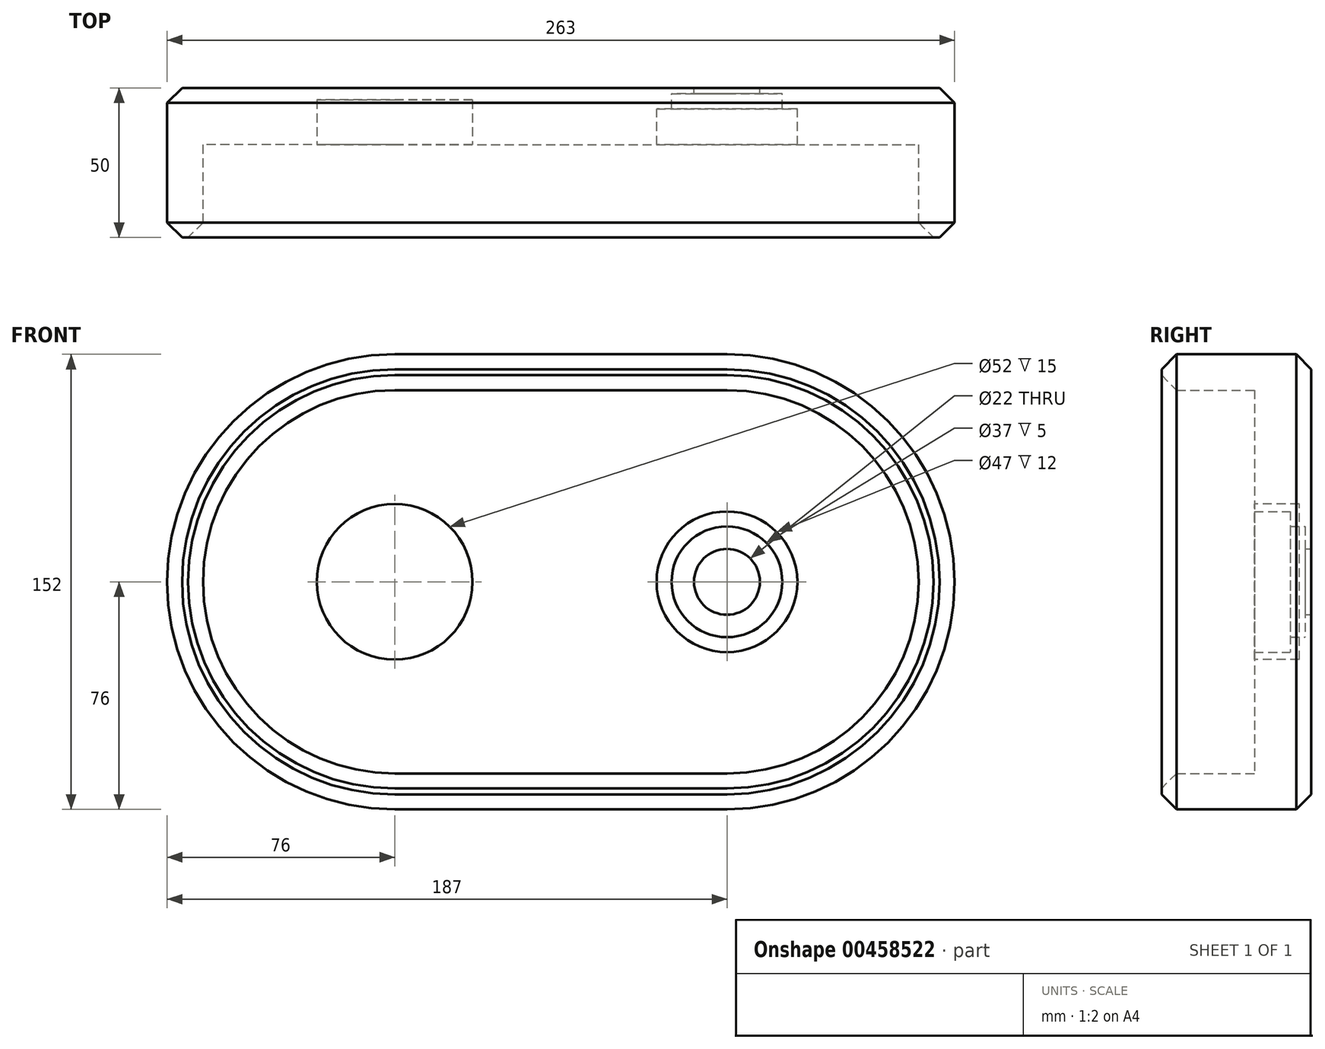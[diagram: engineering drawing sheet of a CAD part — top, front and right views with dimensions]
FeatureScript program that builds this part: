
annotation { "Feature Type Name" : "Feature", "Feature Type Description" : "" }
export const myFeature = defineFeature(function(context is Context, id is Id, definition is map)
    precondition{}
    {
        {
            var Q0;
            Q0=qCreatedBy(makeId("Front.planeOp"),FACE);
            var sketch = newSketch(context, id + "F0", { "sketchPlane" : qUnion([Q0])});
            skArc(sketch, "E0", {"start": v(0, 76) * mm, "mid": v(-76, 0) * mm, "end": v(0, -76) * mm});
            skLineSegment(sketch, "E1", {"start": v(0, 0) * mm, "end": v(204.87, 0) * mm, "construction": true});
            skArc(sketch, "E2", {"start": v(111, -76) * mm, "mid": v(187, 0) * mm, "end": v(111, 76) * mm});
            skLineSegment(sketch, "E3", {"start": v(0, 76) * mm, "end": v(111, 76) * mm});
            skLineSegment(sketch, "E4", {"start": v(0, -76) * mm, "end": v(111, -76) * mm});
            skSolve(sketch);
        }
        {
            var Q0;
            Q0=makeQuery(id+"F0.imprint","IMPRINT",FACE,{"disambiguationData":[TD([[makeQuery(id+"F0.imprint","IMPRINT",EDGE,{"derivedFrom":sQuery(id+"F0.wireOp",EDGE,"E0")}),1.0]])]});
            extrude(context, id + "F1", {"entities" : qUnion([Q0]), "depth" : 50 * mm, "offsetDistance" : 25 * mm});
        }
        {
            var Q0;
            Q0=qCreatedBy(makeId("Front.planeOp"),FACE);
            cPlane(context, id + "F2", {"entities" : qUnion([Q0]), "cplaneType" : CPlaneType.OFFSET, "offset" : 19 * mm, "width" : 150 * mm, "height" : 150 * mm});
        }
        {
            var Q0;
            Q0=qCreatedBy(id+"F2.planeOp",FACE);
            var sketch = newSketch(context, id + "F3", { "sketchPlane" : qUnion([Q0])});
            skArc(sketch, "E5", {"start": v(0, 64) * mm, "mid": v(-64, 0) * mm, "end": v(0, -64) * mm});
            skLineSegment(sketch, "E6", {"start": v(0, 0) * mm, "end": v(196.84, 0) * mm, "construction": true});
            skArc(sketch, "E7", {"start": v(111, -64) * mm, "mid": v(175, 0) * mm, "end": v(111, 64) * mm});
            skLineSegment(sketch, "E8", {"start": v(0, 64) * mm, "end": v(111, 64) * mm});
            skLineSegment(sketch, "E9", {"start": v(0, -64) * mm, "end": v(111, -64) * mm});
            skSolve(sketch);
        }
        {
            var Q0;
            Q0 = qSketchRegion(id + "F3", true);
            var Q1;
            Q1=makeQuery(id+"F1.opExtrude","CAP_FACE",FACE,{"disambiguationData":[OSD([sQuery(id+"F0.wireOp",EDGE,"E0"),sQuery(id+"F0.wireOp",EDGE,"E2"),sQuery(id+"F0.wireOp",EDGE,"E3"),sQuery(id+"F0.wireOp",EDGE,"E4")])],"isStart":false});
            extrude(context, id + "F4", {"entities" : qUnion([Q0, Q1]), "operationType" : NewBodyOperationType.REMOVE, "depth" : 60 * mm, "offsetDistance" : 25 * mm});
        }
        {
            var Q0;
            Q0=qCreatedBy(id+"F2.planeOp",FACE);
            var sketch = newSketch(context, id + "F5", { "sketchPlane" : qUnion([Q0])});
            skCircle(sketch, "E10", {"center": v(0, 0) * mm, "radius": 26 * mm});
            skSolve(sketch);
        }
        {
            var Q0;
            Q0 = qSketchRegion(id + "F5", true);
            var Q1;
            Q1=makeQuery(id+"F5.imprint","IMPRINT",FACE,{"disambiguationData":[TD([[makeQuery(id+"F5.imprint","IMPRINT",EDGE,{"derivedFrom":sQuery(id+"F5.wireOp",EDGE,"E10")}),1.0]])]});
            extrude(context, id + "F6", {"entities" : qUnion([Q0, Q1]), "operationType" : NewBodyOperationType.REMOVE, "oppositeDirection" : true, "depth" : 15 * mm, "offsetDistance" : 25 * mm});
        }
        {
            var Q0;
            Q0=qCreatedBy(makeId("Right.planeOp"),FACE);
            cPlane(context, id + "F7", {"entities" : qUnion([Q0]), "cplaneType" : CPlaneType.OFFSET, "offset" : 111 * mm, "width" : 150 * mm, "height" : 150 * mm});
        }
        {
            var Q0;
            Q0=qCreatedBy(id+"F7.planeOp",FACE);
            var sketch = newSketch(context, id + "F8", { "sketchPlane" : qUnion([Q0])});
            skLineSegment(sketch, "E11", {"start": v(0, 11) * mm, "end": v(-2, 11) * mm});
            skLineSegment(sketch, "E12", {"start": v(-2, 11) * mm, "end": v(-2, 18.5) * mm});
            skLineSegment(sketch, "E13", {"start": v(-2, 18.5) * mm, "end": v(-7, 18.5) * mm});
            skLineSegment(sketch, "E14", {"start": v(-7, 18.5) * mm, "end": v(-7, 23.5) * mm});
            skLineSegment(sketch, "E15", {"start": v(-7, 23.5) * mm, "end": v(-19, 23.5) * mm});
            skLineSegment(sketch, "E16", {"start": v(-19, 23.5) * mm, "end": v(-19, 0) * mm});
            skLineSegment(sketch, "E17", {"start": v(-19, 0) * mm, "end": v(0, 0) * mm, "construction": true});
            skLineSegment(sketch, "E18", {"start": v(0, 0) * mm, "end": v(0, 11) * mm});
            skLineSegment(sketch, "E19", {"start": v(-19, 0) * mm, "end": v(0, 0) * mm});
            skSolve(sketch);
        }
        {
            var Q0;
            Q0 = qSketchRegion(id + "F8", true);
            var Q1;
            Q1=sQuery(id+"F8.wireOp",EDGE,"E17");
            revolve(context, id + "F9", {"operationType" : NewBodyOperationType.REMOVE, "entities" : qUnion([Q0]), "axis" : qUnion([Q1]), "revolveType" : RevolveType.FULL, "oppositeDirection" : true});
        }
        {
            var Q0;
            Q0=makeQuery(id+"F1.opExtrude","CAP_EDGE",EDGE,{"disambiguationData":[OSD([sQuery(id+"F0.wireOp",EDGE,"E3")])],"isStart":true});
            var Q1;
            Q1=makeQuery(id+"F1.opExtrude","CAP_EDGE",EDGE,{"disambiguationData":[OSD([sQuery(id+"F0.wireOp",EDGE,"E2")])],"isStart":true});
            var Q2;
            Q2=makeQuery(id+"F1.opExtrude","CAP_EDGE",EDGE,{"disambiguationData":[OSD([sQuery(id+"F0.wireOp",EDGE,"E0")])],"isStart":true});
            var Q3;
            Q3=makeQuery(id+"F1.opExtrude","CAP_EDGE",EDGE,{"disambiguationData":[OSD([sQuery(id+"F0.wireOp",EDGE,"E4")])],"isStart":true});
            chamfer(context, id + "F10", {"entities" : qUnion([Q0, Q1, Q2, Q3]), "width" : 5 * mm, "tangentPropagation" : true});
        }
        {
            var Q0;
            Q0=makeQuery(id+"F1.opExtrude","CAP_EDGE",EDGE,{"disambiguationData":[OSD([sQuery(id+"F0.wireOp",EDGE,"E3")])],"isStart":false});
            var Q1;
            Q1=makeQuery(id+"F1.opExtrude","CAP_EDGE",EDGE,{"disambiguationData":[OSD([sQuery(id+"F0.wireOp",EDGE,"E0")])],"isStart":false});
            var Q2;
            Q2=makeQuery(id+"F1.opExtrude","CAP_EDGE",EDGE,{"disambiguationData":[OSD([sQuery(id+"F0.wireOp",EDGE,"E2")])],"isStart":false});
            var Q3;
            Q3=makeQuery(id+"F1.opExtrude","CAP_EDGE",EDGE,{"disambiguationData":[OSD([sQuery(id+"F0.wireOp",EDGE,"E4")])],"isStart":false});
            chamfer(context, id + "F11", {"entities" : qUnion([Q0, Q1, Q2, Q3]), "width" : 5 * mm, "tangentPropagation" : true});
        }
        {
            var Q0;
            {var subQ0=sQuery(id+"F0.wireOp",EDGE,"E4");var subQ1=sQuery(id+"F0.wireOp",EDGE,"E3");var subQ2=sQuery(id+"F0.wireOp",EDGE,"E2");var subQ3=sQuery(id+"F0.wireOp",EDGE,"E0");Q0=makeQuery(id+"F4.boolean.opBoolean","INTERSECT",EDGE,{"derivedFrom":[makeQuery(id+"F1.opExtrude","CAP_FACE",FACE,{"disambiguationData":[OSD([subQ3,subQ2,subQ1,subQ0])],"isStart":false}),makeQuery(id+"F4.opExtrude","CAP_FACE",FACE,{"disambiguationData":[OSD([subQ3,subQ2,subQ1,subQ0])],"isStart":true}),makeQuery(id+"F4.opExtrude","SWEPT_FACE",FACE,{"disambiguationData":[OSD([sQuery(id+"F3.wireOp",EDGE,"E8")])]})]});}
            var Q1;
            {var subQ0=sQuery(id+"F0.wireOp",EDGE,"E4");var subQ1=sQuery(id+"F0.wireOp",EDGE,"E3");var subQ2=sQuery(id+"F0.wireOp",EDGE,"E2");var subQ3=sQuery(id+"F0.wireOp",EDGE,"E0");Q1=makeQuery(id+"F4.boolean.opBoolean","INTERSECT",EDGE,{"derivedFrom":[makeQuery(id+"F1.opExtrude","CAP_FACE",FACE,{"disambiguationData":[OSD([subQ3,subQ2,subQ1,subQ0])],"isStart":false}),makeQuery(id+"F4.opExtrude","CAP_FACE",FACE,{"disambiguationData":[OSD([subQ3,subQ2,subQ1,subQ0])],"isStart":true}),makeQuery(id+"F4.opExtrude","SWEPT_FACE",FACE,{"disambiguationData":[OSD([sQuery(id+"F3.wireOp",EDGE,"E5")])]})]});}
            var Q2;
            {var subQ0=sQuery(id+"F0.wireOp",EDGE,"E4");var subQ1=sQuery(id+"F0.wireOp",EDGE,"E3");var subQ2=sQuery(id+"F0.wireOp",EDGE,"E2");var subQ3=sQuery(id+"F0.wireOp",EDGE,"E0");Q2=makeQuery(id+"F4.boolean.opBoolean","INTERSECT",EDGE,{"derivedFrom":[makeQuery(id+"F1.opExtrude","CAP_FACE",FACE,{"disambiguationData":[OSD([subQ3,subQ2,subQ1,subQ0])],"isStart":false}),makeQuery(id+"F4.opExtrude","CAP_FACE",FACE,{"disambiguationData":[OSD([subQ3,subQ2,subQ1,subQ0])],"isStart":true}),makeQuery(id+"F4.opExtrude","SWEPT_FACE",FACE,{"disambiguationData":[OSD([sQuery(id+"F3.wireOp",EDGE,"E7")])]})]});}
            var Q3;
            {var subQ0=sQuery(id+"F0.wireOp",EDGE,"E4");var subQ1=sQuery(id+"F0.wireOp",EDGE,"E3");var subQ2=sQuery(id+"F0.wireOp",EDGE,"E2");var subQ3=sQuery(id+"F0.wireOp",EDGE,"E0");Q3=makeQuery(id+"F4.boolean.opBoolean","INTERSECT",EDGE,{"derivedFrom":[makeQuery(id+"F1.opExtrude","CAP_FACE",FACE,{"disambiguationData":[OSD([subQ3,subQ2,subQ1,subQ0])],"isStart":false}),makeQuery(id+"F4.opExtrude","CAP_FACE",FACE,{"disambiguationData":[OSD([subQ3,subQ2,subQ1,subQ0])],"isStart":true}),makeQuery(id+"F4.opExtrude","SWEPT_FACE",FACE,{"disambiguationData":[OSD([sQuery(id+"F3.wireOp",EDGE,"E9")])]})]});}
            chamfer(context, id + "F12", {"entities" : qUnion([Q0, Q1, Q2, Q3]), "width" : 5 * mm, "tangentPropagation" : true});
        }
    });
